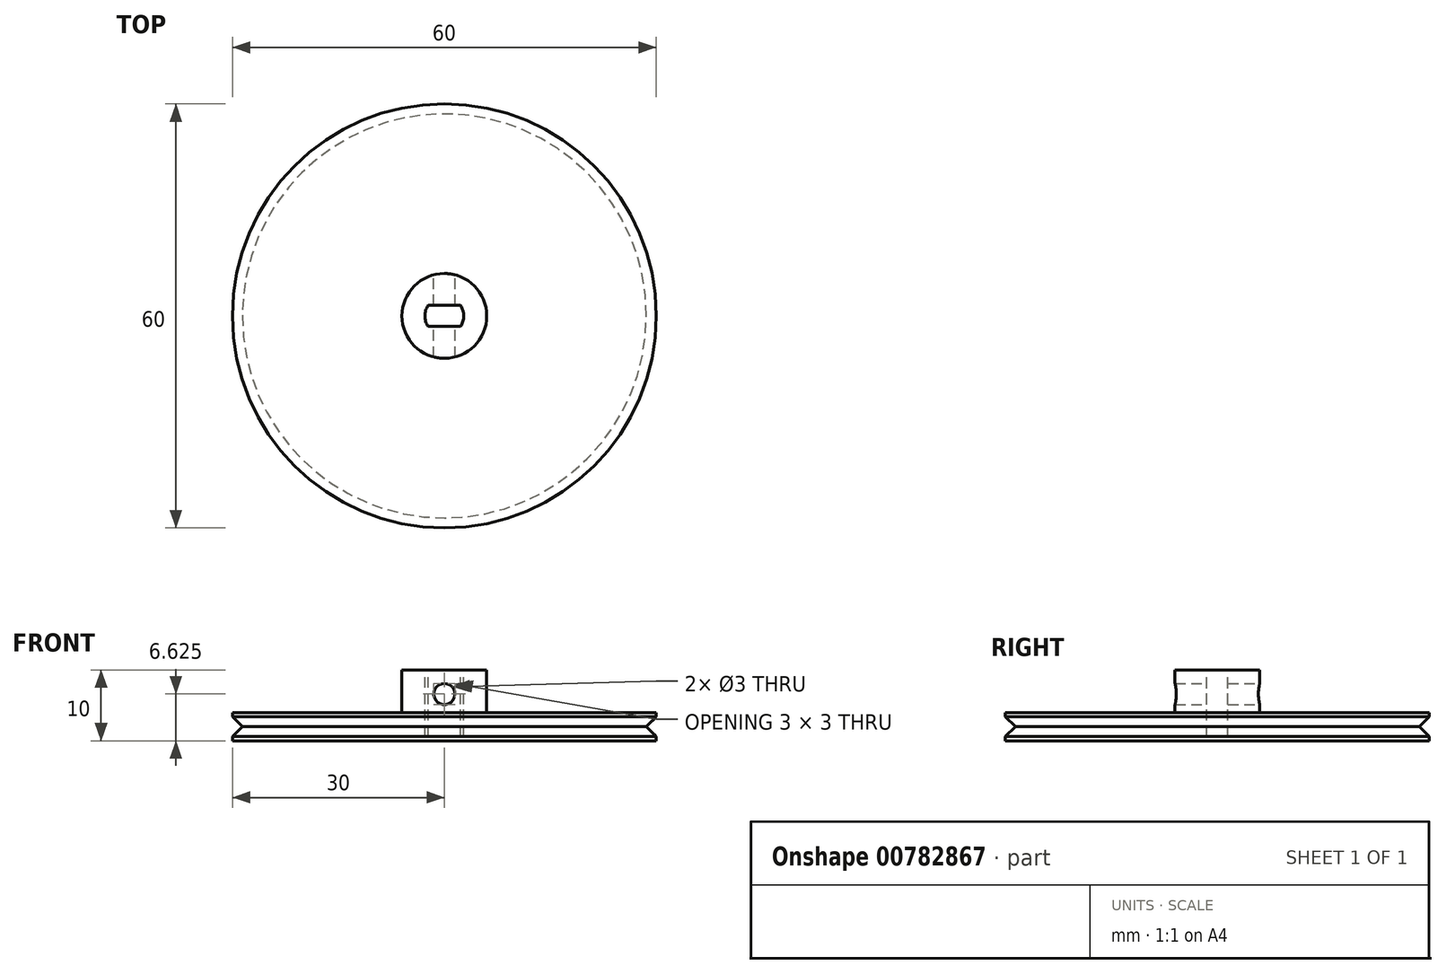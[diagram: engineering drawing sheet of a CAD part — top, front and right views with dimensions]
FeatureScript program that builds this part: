
annotation { "Feature Type Name" : "Feature", "Feature Type Description" : "" }
export const myFeature = defineFeature(function(context is Context, id is Id, definition is map)
    precondition{}
    {
        {
            var Q0;
            Q0=qCreatedBy(makeId("Top.planeOp"),FACE);
            var sketch = newSketch(context, id + "F0", { "sketchPlane" : qUnion([Q0])});
            skCircle(sketch, "E0", {"center": v(0, 0) * mm, "radius": 30 * mm});
            skSolve(sketch);
        }
        {
            var Q0;
            Q0 = qSketchRegion(id + "F0", true);
            extrude(context, id + "F1", {"entities" : qUnion([Q0]), "depth" : 4 * mm, "offsetDistance" : 25 * mm});
        }
        {
            var Q0;
            Q0=makeQuery(id+"F1.opExtrude","CAP_FACE",FACE,{"disambiguationData":[OSD([sQuery(id+"F0.wireOp",EDGE,"E0")])],"isStart":false});
            var sketch = newSketch(context, id + "F2", { "sketchPlane" : qUnion([Q0])});
            skCircle(sketch, "E1", {"center": v(0, 0) * mm, "radius": 6 * mm});
            skSolve(sketch);
        }
        {
            var Q0;
            Q0 = qSketchRegion(id + "F2", true);
            extrude(context, id + "F3", {"entities" : qUnion([Q0]), "operationType" : NewBodyOperationType.ADD, "depth" : 6 * mm, "offsetDistance" : 25 * mm});
        }
        {
            var Q0;
            Q0=qCreatedBy(makeId("Front.planeOp"),FACE);
            var sketch = newSketch(context, id + "F4", { "sketchPlane" : qUnion([Q0])});
            skCircle(sketch, "E2", {"center": v(0, 6.63) * mm, "radius": 1.5 * mm});
            skSolve(sketch);
        }
        {
            var Q0;
            Q0 = qSketchRegion(id + "F4", true);
            extrude(context, id + "F5", {"entities" : qUnion([Q0]), "operationType" : NewBodyOperationType.REMOVE, "endBound" : BoundingType.SYMMETRIC, "depth" : 25 * mm, "offsetDistance" : 25 * mm});
        }
        {
            var Q0;
            Q0=makeQuery(id+"F3.opExtrude","CAP_FACE",FACE,{"disambiguationData":[OSD([sQuery(id+"F2.wireOp",EDGE,"E1")])],"isStart":false});
            var sketch = newSketch(context, id + "F6", { "sketchPlane" : qUnion([Q0])});
            skLineSegment(sketch, "E3.bottom", {"start": v(-2.3, -1.5) * mm, "end": v(2.3, -1.5) * mm});
            skLineSegment(sketch, "E3.top", {"start": v(-2.3, 1.5) * mm, "end": v(2.3, 1.5) * mm});
            skLineSegment(sketch, "E3.left", {"start": v(-2.3, -1.5) * mm, "end": v(-2.3, 1.5) * mm});
            skLineSegment(sketch, "E3.right", {"start": v(2.3, -1.5) * mm, "end": v(2.3, 1.5) * mm});
            skPoint(sketch, "E3.middle", {"position": v(0, 0) * mm});
            skArc(sketch, "E4", {"start": v(-2.3, 1.5) * mm, "mid": v(-2.75, 0) * mm, "end": v(-2.3, -1.5) * mm});
            skArc(sketch, "E5", {"start": v(2.3, -1.5) * mm, "mid": v(2.75, 0) * mm, "end": v(2.3, 1.5) * mm});
            skLineSegment(sketch, "E6", {"start": v(-2.75, 0) * mm, "end": v(2.75, 0) * mm, "construction": true});
            skSolve(sketch);
        }
        {
            var Q0;
            Q0 = qSketchRegion(id + "F6", true);
            extrude(context, id + "F7", {"entities" : qUnion([Q0]), "operationType" : NewBodyOperationType.REMOVE, "oppositeDirection" : true, "depth" : 9.4 * mm, "offsetDistance" : 25 * mm});
        }
        {
            var Q0;
            Q0=qCreatedBy(makeId("Front.planeOp"),FACE);
            var sketch = newSketch(context, id + "F8", { "sketchPlane" : qUnion([Q0])});
            skLineSegment(sketch, "E7", {"start": v(30, 3.41) * mm, "end": v(30, 0.59) * mm});
            skLineSegment(sketch, "E8", {"start": v(30, 3.41) * mm, "end": v(28.59, 2) * mm});
            skLineSegment(sketch, "E9", {"start": v(28.59, 2) * mm, "end": v(30, 0.59) * mm});
            skLineSegment(sketch, "E10", {"start": v(30, 2) * mm, "end": v(27.98, 2) * mm, "construction": true});
            skLineSegment(sketch, "E11", {"start": v(30, 4) * mm, "end": v(30, 0) * mm, "construction": true});
            skSolve(sketch);
        }
        {
            var Q0;
            Q0=qCreatedBy(makeId("Front.planeOp"),FACE);
            var sketch = newSketch(context, id + "F9", { "sketchPlane" : qUnion([Q0])});
            skLineSegment(sketch, "E12", {"start": v(0, -8.38) * mm, "end": v(0, 14.25) * mm, "construction": true});
            skSolve(sketch);
        }
        {
            var Q0;
            Q0 = qSketchRegion(id + "F8", true);
            var Q1;
            Q1=sQuery(id+"F9.wireOp",EDGE,"E12");
            revolve(context, id + "F10", {"operationType" : NewBodyOperationType.REMOVE, "surfaceOperationType" : NewSurfaceOperationType.NEW, "entities" : qUnion([Q0]), "axis" : qUnion([Q1]), "revolveType" : RevolveType.FULL, "oppositeDirection" : true});
        }
    });
